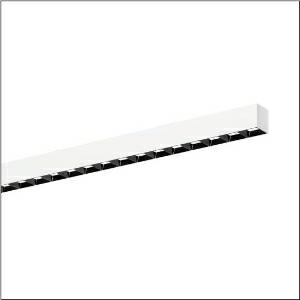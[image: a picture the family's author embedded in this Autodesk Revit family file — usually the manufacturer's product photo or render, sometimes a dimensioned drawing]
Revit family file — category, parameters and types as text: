
# Revit family: silica_r__21_51mx21tctaw_c13c
name_source: partatom
category: Lighting Fixtures
units: mm (PartAtom-declared; Revit-internal decimal feet)

## family parameters
Cut with Voids When Loaded = No
Host = Face
Light Source = No
Part Type = Normal
Room Calculation Point = No
Round Connector Dimension = Use Diameter
Shared = No

## types (1)
- --- (1 x LED, 9300 lm, 80.5 W, 6500K)
    Apparent Load = 81 VA
    CIE Flux Codes = 85 99 100 100 100
    Color Rendering = 80
    Color Temperature = 6500K
    Default Elevation = 1800 mm
    Description = Silica® 21, office luminaire, primary light control with darklight reflector, of PMMA, black, CAT 2 (L<= 3000cd/m²), light emission: direct distribution, primary light characteristic: symmetric, installation type: surface-mounted, LED, rated luminous flux: 9.300lm, luminous efficacy: 110lm/W, light colour: 8tw, colour temperature: 2700..6500K, control gear: DALI DT8, with terminal, 3+2-pole, max. 2.5mm², mains connection: 220..240V, AC, 50/60Hz, rated input power: 84.6W, luminaire housing, of aluminium, traffic white (RAL 9016), length: 3.004mm, width: 53mm, height: 53mm, protection rating (complete): IP20, insulation class (complete): insulation class I (protective earthing), certification: CE, permissible operating ambient temperature: 0..+35°C, standard: EN 50419, packaging unit: 1 piece
    Height = 53 mm
    Lamp = 1 x LED
    Lamp Light Flux = 9300 lm
    Lamp Power = 80.5 W
    Lamp count = 1
    Length = 3004 mm
    Luminous efficacy = 116 lm/W
    Manufacturer = Siteco
    ModVariant = No
    Model = 51MX21TCTAW
    Mounting Place = Ceiling
    Mounting Type = Surface mounted
    Number of Poles = 1
    OnlyDefault = Yes
    Power Factor = 1
    Product Name = Silica® 21
    Product group = office luminaire | ceiling mounted
    ProductGroupID = 302
    Protection Class = Protection class I
    Protection Degree = IP 20
    RLX_Detail_Level = 1
    RLX_Emergency_Light_Flux = 0 lm
    RLX_Emergency_Type = 0
    RLX_Emergency_Type_DB = No
    RlxData = <blob elided: 58933 chars, md5=eb470fda>
    Socket = socket
    Standby Power = 0 W
    System Light Flux = 9300 lm
    System Power = 81 W
    Type Comments = individual setting
    Type Image = l_1335873.jpg
    URL = http://relux.com
    VarID = @adj_140076
    Voltage = 0 V
    Weight = 0.00 kg
    Width = 53 mm

## geometry (parser evidence)
native form markers: Blend x4, Sweep x10
no freeform markers — native parametric forms only
